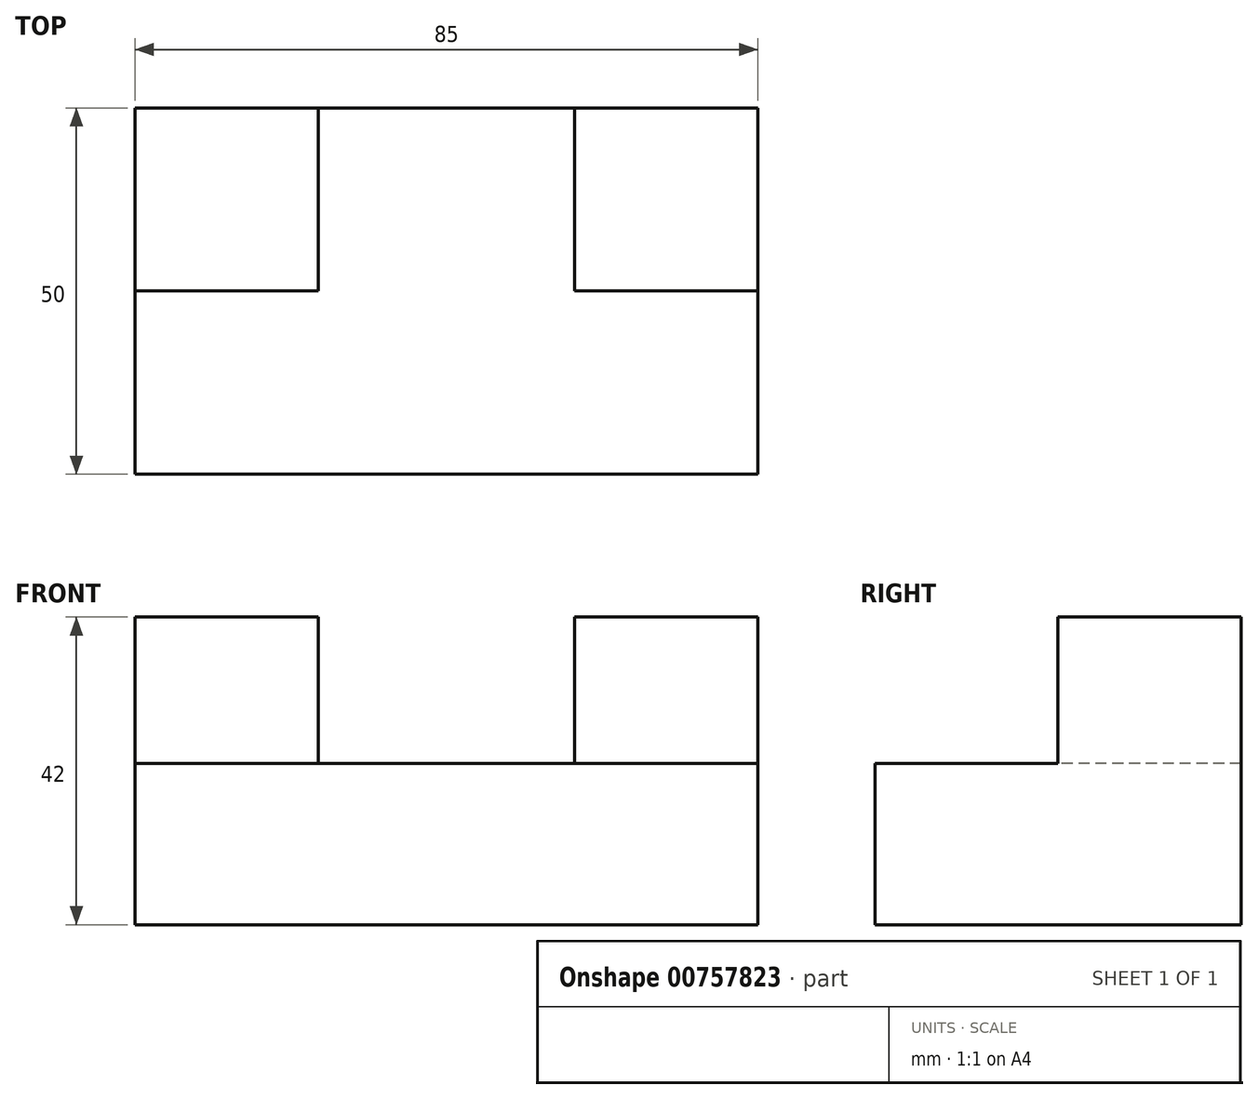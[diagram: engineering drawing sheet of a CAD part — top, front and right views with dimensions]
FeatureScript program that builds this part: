
annotation { "Feature Type Name" : "Feature", "Feature Type Description" : "" }
export const myFeature = defineFeature(function(context is Context, id is Id, definition is map)
    precondition{}
    {
        {
            var Q0;
            Q0=qCreatedBy(makeId("Top.planeOp"),FACE);
            var sketch = newSketch(context, id + "F0", { "sketchPlane" : qUnion([Q0])});
            skLineSegment(sketch, "E0", {"start": v(-42.5, 0) * mm, "end": v(42.5, 0) * mm});
            skLineSegment(sketch, "E1", {"start": v(42.5, 0) * mm, "end": v(42.5, 50) * mm});
            skLineSegment(sketch, "E2", {"start": v(42.5, 50) * mm, "end": v(-42.5, 50) * mm});
            skLineSegment(sketch, "E3", {"start": v(-42.5, 50) * mm, "end": v(-42.5, 0) * mm});
            skLineSegment(sketch, "E4", {"start": v(-42.5, 25) * mm, "end": v(-17.5, 25) * mm});
            skLineSegment(sketch, "E5", {"start": v(-17.5, 25) * mm, "end": v(-17.5, 50) * mm});
            skLineSegment(sketch, "E6", {"start": v(17.5, 50) * mm, "end": v(17.5, 25) * mm});
            skLineSegment(sketch, "E7", {"start": v(17.5, 25) * mm, "end": v(42.5, 25) * mm});
            skSolve(sketch);
        }
        {
            var Q0;
            {var subQ1=sQuery(id+"F0.wireOp",EDGE,"E0");Q0=makeQuery(id+"F0.imprint","IMPRINT",FACE,{"disambiguationData":[TD([[makeQuery(id+"F0.imprint","IMPRINT",EDGE,{"derivedFrom":subQ1}),1.0]])]});}
            extrude(context, id + "F1", {"entities" : qUnion([Q0]), "depth" : 22 * mm, "offsetDistance" : 25 * mm});
        }
        {
            var Q0;
            {var subQ4=sQuery(id+"F0.wireOp",EDGE,"E4");Q0=makeQuery(id+"F0.imprint","IMPRINT",FACE,{"disambiguationData":[TD([[makeQuery(id+"F0.imprint","IMPRINT",EDGE,{"derivedFrom":subQ4}),1.0]])]});}
            var Q1;
            {var subQ4=sQuery(id+"F0.wireOp",EDGE,"E6");Q1=makeQuery(id+"F0.imprint","IMPRINT",FACE,{"disambiguationData":[TD([[makeQuery(id+"F0.imprint","IMPRINT",EDGE,{"derivedFrom":subQ4}),1.0]])]});}
            extrude(context, id + "F2", {"entities" : qUnion([Q0, Q1]), "operationType" : NewBodyOperationType.ADD, "depth" : 42 * mm, "offsetDistance" : 25 * mm});
        }
    });
